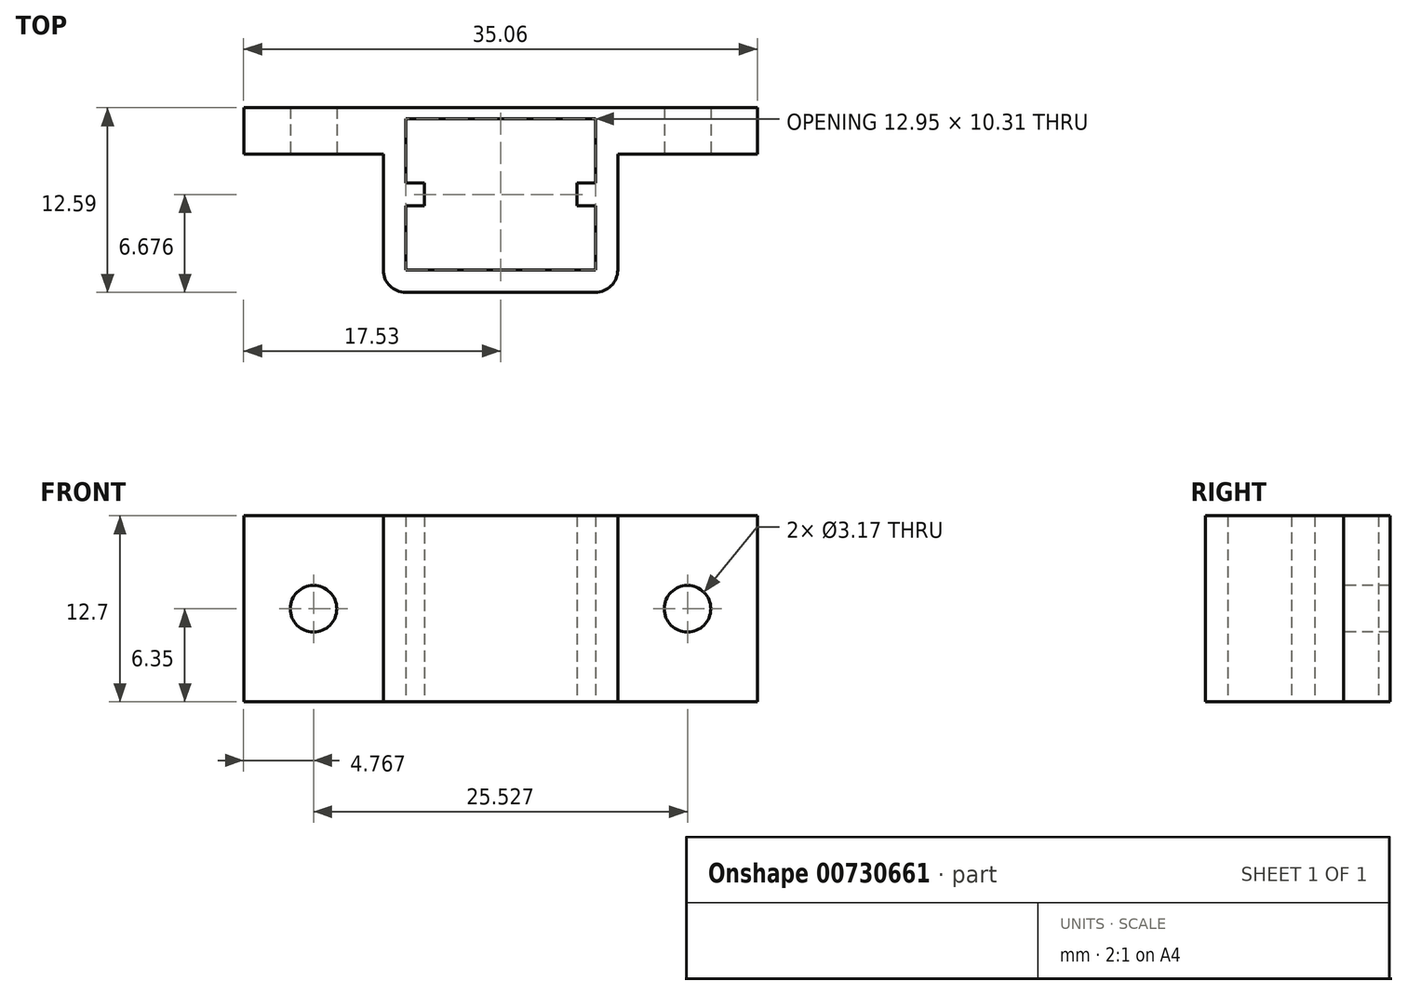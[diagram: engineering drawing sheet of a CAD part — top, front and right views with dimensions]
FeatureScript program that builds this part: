
annotation { "Feature Type Name" : "Feature", "Feature Type Description" : "" }
export const myFeature = defineFeature(function(context is Context, id is Id, definition is map)
    precondition{}
    {
        {
            var Q0;
            Q0=qCreatedBy(makeId("Top.planeOp"),FACE);
            var sketch = newSketch(context, id + "F0", { "sketchPlane" : qUnion([Q0])});
            skLineSegment(sketch, "E0", {"start": v(6.48, 0) * mm, "end": v(-6.48, 0) * mm});
            skLineSegment(sketch, "E1", {"start": v(-6.48, 0) * mm, "end": v(-6.48, 4.37) * mm});
            skLineSegment(sketch, "E2", {"start": v(-6.48, 10.31) * mm, "end": v(6.48, 10.31) * mm});
            skLineSegment(sketch, "E3", {"start": v(6.48, 10.31) * mm, "end": v(6.48, 5.94) * mm});
            skLineSegment(sketch, "E4", {"start": v(-6.48, 4.37) * mm, "end": v(-5.2, 4.37) * mm});
            skLineSegment(sketch, "E5", {"start": v(-5.2, 4.37) * mm, "end": v(-5.2, 5.94) * mm});
            skLineSegment(sketch, "E6", {"start": v(-5.2, 5.94) * mm, "end": v(-6.48, 5.94) * mm});
            skLineSegment(sketch, "E7", {"start": v(6.48, 5.94) * mm, "end": v(5.2, 5.94) * mm});
            skLineSegment(sketch, "E8", {"start": v(5.2, 5.94) * mm, "end": v(5.2, 4.37) * mm});
            skLineSegment(sketch, "E9", {"start": v(5.2, 4.37) * mm, "end": v(6.48, 4.37) * mm});
            skLineSegment(sketch, "E10.bottom", {"start": v(-8, -1.52) * mm, "end": v(8, -1.52) * mm});
            skLineSegment(sketch, "E10.top", {"start": v(-8, 11.07) * mm, "end": v(8, 11.07) * mm});
            skLineSegment(sketch, "E10.left", {"start": v(-8, -1.52) * mm, "end": v(-8, 11.07) * mm});
            skLineSegment(sketch, "E10.right", {"start": v(8, -1.52) * mm, "end": v(8, 11.07) * mm});
            skLineSegment(sketch, "E11", {"start": v(0, 10.31) * mm, "end": v(0, 11.07) * mm, "construction": true});
            skLineSegment(sketch, "E12.trimOffspring", {"start": v(-6.48, 5.94) * mm, "end": v(-6.48, 10.31) * mm});
            skLineSegment(sketch, "E13.trimOffspring", {"start": v(6.48, 4.37) * mm, "end": v(6.48, 0) * mm});
            skSolve(sketch);
        }
        {
            var Q0;
            Q0 = qSketchRegion(id + "F0", true);
            extrude(context, id + "F1", {"entities" : qUnion([Q0]), "depth" : 12.7 * mm, "offsetDistance" : 25.4 * mm});
        }
        {
            var Q0;
            Q0=makeQuery(id+"F1.opExtrude","SWEPT_FACE",FACE,{"disambiguationData":[OSD([sQuery(id+"F0.wireOp",EDGE,"E10.top")])]});
            var sketch = newSketch(context, id + "F2", { "sketchPlane" : qUnion([Q0])});
            skLineSegment(sketch, "E14.bottom", {"start": v(8, 0) * mm, "end": v(17.53, 0) * mm});
            skLineSegment(sketch, "E14.top", {"start": v(8, 12.7) * mm, "end": v(17.53, 12.7) * mm});
            skLineSegment(sketch, "E14.left", {"start": v(8, 0) * mm, "end": v(8, 12.7) * mm});
            skLineSegment(sketch, "E14.right", {"start": v(17.53, 0) * mm, "end": v(17.53, 12.7) * mm});
            skLineSegment(sketch, "E15.bottom", {"start": v(-8, 0) * mm, "end": v(-17.53, 0) * mm});
            skLineSegment(sketch, "E15.top", {"start": v(-8, 12.7) * mm, "end": v(-17.53, 12.7) * mm});
            skLineSegment(sketch, "E15.left", {"start": v(-8, 0) * mm, "end": v(-8, 12.7) * mm});
            skLineSegment(sketch, "E15.right", {"start": v(-17.53, 0) * mm, "end": v(-17.53, 12.7) * mm});
            skSolve(sketch);
        }
        {
            var Q0;
            Q0 = qSketchRegion(id + "F2", true);
            extrude(context, id + "F3", {"entities" : qUnion([Q0]), "operationType" : NewBodyOperationType.ADD, "oppositeDirection" : true, "depth" : 3.17 * mm, "offsetDistance" : 25.4 * mm});
        }
        {
            var Q0;
            Q0=makeQuery(id+"F1.opExtrude","SWEPT_EDGE",EDGE,{"disambiguationData":[OSD([sQuery(id+"F0.wireOp",EDGE,"E10.bottom"),sQuery(id+"F0.wireOp",EDGE,"E10.left")])]});
            var Q1;
            Q1=makeQuery(id+"F1.opExtrude","SWEPT_EDGE",EDGE,{"disambiguationData":[OSD([sQuery(id+"F0.wireOp",EDGE,"E10.bottom"),sQuery(id+"F0.wireOp",EDGE,"E10.right")])]});
            fillet(context, id + "F4", {"entities" : qUnion([Q0, Q1]), "radius" : 1.52 * mm, "tangentPropagation" : true, "allowEdgeOverflow" : false});
        }
        {
            var Q0;
            Q0=makeQuery(id+"F3.opExtrude","CAP_FACE",FACE,{"disambiguationData":[OSD([sQuery(id+"F2.wireOp",EDGE,"E14.bottom"),sQuery(id+"F2.wireOp",EDGE,"E14.top"),sQuery(id+"F2.wireOp",EDGE,"E14.left"),sQuery(id+"F2.wireOp",EDGE,"E14.right")])],"isStart":false});
            var sketch = newSketch(context, id + "F5", { "sketchPlane" : qUnion([Q0])});
            skCircle(sketch, "E16", {"center": v(-12.76, 6.35) * mm, "radius": 1.59 * mm});
            skCircle(sketch, "E17", {"center": v(12.76, 6.35) * mm, "radius": 1.59 * mm});
            skLineSegment(sketch, "E18", {"start": v(-8, 12.7) * mm, "end": v(-17.53, 0) * mm, "construction": true});
            skLineSegment(sketch, "E19", {"start": v(8, 12.7) * mm, "end": v(17.53, 0) * mm, "construction": true});
            skSolve(sketch);
        }
        {
            var Q0;
            Q0 = qSketchRegion(id + "F5", true);
            extrude(context, id + "F6", {"entities" : qUnion([Q0]), "operationType" : NewBodyOperationType.REMOVE, "oppositeDirection" : true, "depth" : 25.4 * mm, "offsetDistance" : 25.4 * mm});
        }
    });
